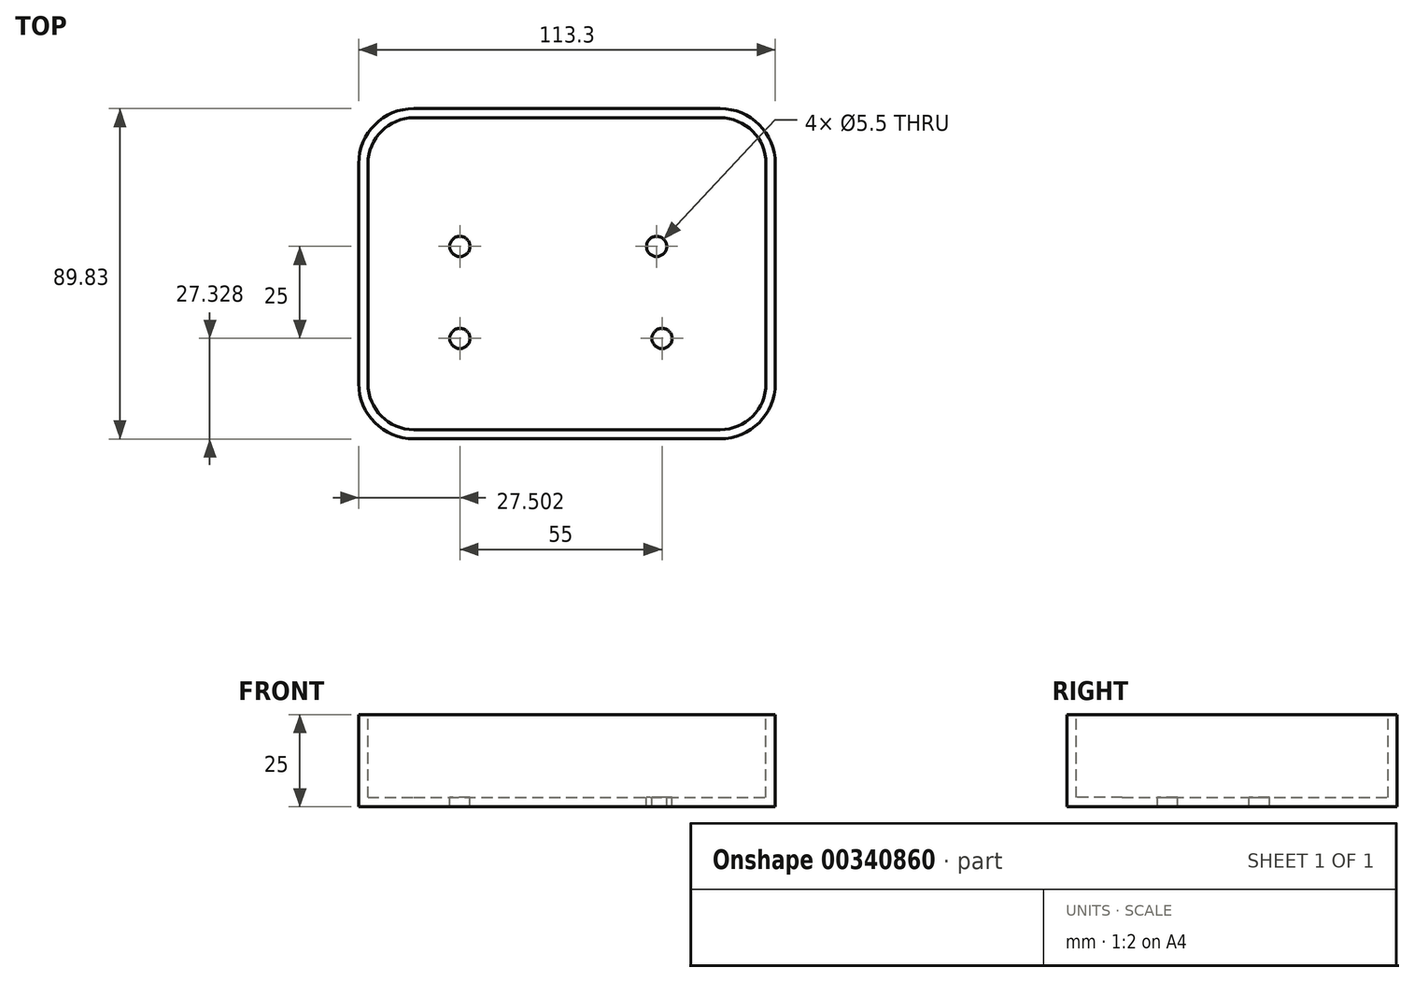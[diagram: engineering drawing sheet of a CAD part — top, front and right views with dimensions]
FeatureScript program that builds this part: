
annotation { "Feature Type Name" : "Feature", "Feature Type Description" : "" }
export const myFeature = defineFeature(function(context is Context, id is Id, definition is map)
    precondition{}
    {
        {
            var Q0;
            Q0=qCreatedBy(makeId("Top.planeOp"),FACE);
            var sketch = newSketch(context, id + "F0", { "sketchPlane" : qUnion([Q0])});
            skLineSegment(sketch, "E0.bottom", {"start": v(-59.12, -58.55) * mm, "end": v(54.18, -58.55) * mm});
            skLineSegment(sketch, "E0.top", {"start": v(-59.12, 31.28) * mm, "end": v(54.18, 31.28) * mm});
            skLineSegment(sketch, "E0.left", {"start": v(-59.12, -58.55) * mm, "end": v(-59.12, 31.28) * mm});
            skLineSegment(sketch, "E0.right", {"start": v(54.18, -58.55) * mm, "end": v(54.18, 31.28) * mm});
            skSolve(sketch);
        }
        {
            var Q0;
            Q0=makeQuery(id+"F0.imprint","IMPRINT",FACE,{"disambiguationData":[TD([[makeQuery(id+"F0.imprint","IMPRINT",EDGE,{"derivedFrom":sQuery(id+"F0.wireOp",EDGE,"E0.bottom")}),1.0]])]});
            extrude(context, id + "F1", {"entities" : qUnion([Q0]), "depth" : 25 * mm, "offsetDistance" : 25 * mm});
        }
        {
            var Q0;
            Q0=makeQuery(id+"F1.opExtrude","SWEPT_EDGE",EDGE,{"disambiguationData":[OSD([sQuery(id+"F0.wireOp",EDGE,"E0.bottom"),sQuery(id+"F0.wireOp",EDGE,"E0.left")])]});
            var Q1;
            Q1=makeQuery(id+"F1.opExtrude","SWEPT_EDGE",EDGE,{"disambiguationData":[OSD([sQuery(id+"F0.wireOp",EDGE,"E0.bottom"),sQuery(id+"F0.wireOp",EDGE,"E0.right")])]});
            var Q2;
            Q2=makeQuery(id+"F1.opExtrude","SWEPT_EDGE",EDGE,{"disambiguationData":[OSD([sQuery(id+"F0.wireOp",EDGE,"E0.top"),sQuery(id+"F0.wireOp",EDGE,"E0.right")])]});
            var Q3;
            Q3=makeQuery(id+"F1.opExtrude","SWEPT_EDGE",EDGE,{"disambiguationData":[OSD([sQuery(id+"F0.wireOp",EDGE,"E0.top"),sQuery(id+"F0.wireOp",EDGE,"E0.left")])]});
            fillet(context, id + "F2", {"entities" : qUnion([Q0, Q1, Q2, Q3]), "radius" : 15 * mm, "tangentPropagation" : true, "allowEdgeOverflow" : false});
        }
        {
            var Q0;
            Q0=makeQuery(id+"F1.opExtrude","CAP_FACE",FACE,{"disambiguationData":[OSD([sQuery(id+"F0.wireOp",EDGE,"E0.bottom"),sQuery(id+"F0.wireOp",EDGE,"E0.top"),sQuery(id+"F0.wireOp",EDGE,"E0.left"),sQuery(id+"F0.wireOp",EDGE,"E0.right")])],"isStart":false});
            shell(context, id + "F3", {"entities" : qUnion([Q0]), "thickness" : 2.5 * mm});
        }
        {
            var Q0;
            Q0=makeQuery(id+"F3.opShell","OFFSET_FACE",FACE,{"disambiguationData":[OSD([sQuery(id+"F0.wireOp",EDGE,"E0.bottom"),sQuery(id+"F0.wireOp",EDGE,"E0.top"),sQuery(id+"F0.wireOp",EDGE,"E0.left"),sQuery(id+"F0.wireOp",EDGE,"E0.right")])]});
            var sketch = newSketch(context, id + "F4", { "sketchPlane" : qUnion([Q0])});
            skPoint(sketch, "E1", {"position": v(-31.62, -6.22) * mm});
            skPoint(sketch, "E2", {"position": v(21.9, -6.22) * mm});
            skPoint(sketch, "E3", {"position": v(-31.62, -31.22) * mm});
            skPoint(sketch, "E4", {"position": v(23.38, -31.22) * mm});
            skSolve(sketch);
        }
        {
            var Q0;
            Q0=sQuery(id+"F4.wireOp",VERTEX,"E1");
            var Q1;
            Q1=sQuery(id+"F4.wireOp",VERTEX,"E3");
            var Q2;
            Q2=sQuery(id+"F4.wireOp",VERTEX,"E2");
            var Q3;
            Q3=sQuery(id+"F4.wireOp",VERTEX,"E4");
            var Q4;
            Q4=makeQuery(id+"F1.opExtrude","SWEPT_BODY",BODY,{"disambiguationData":[OSD([sQuery(id+"F0.wireOp",EDGE,"E0.bottom"),sQuery(id+"F0.wireOp",EDGE,"E0.top"),sQuery(id+"F0.wireOp",EDGE,"E0.left"),sQuery(id+"F0.wireOp",EDGE,"E0.right")])]});
            hole(context, id + "F5", {"style" : HoleStyle.SIMPLE, "endStyle" : HoleEndStyle.THROUGH, "standardTappedOrClearance" : lookupTablePath({ "standard" : "ISO", "fit" : "Normal", "size" : "M5", "type" : "Clearance" }), "standardBlindInLast" : lookupTablePath({ "fit" : "Standard", "standard" : "ISO", "size" : "M5", "type" : "Clearance" }), "holeDiameter" : 5.5 * mm, "majorDiameter" : 5 * mm, "isTappedThrough" : true, "tappedDepth" : 12 * mm, "tapClearance" : 3, "locations" : qUnion([Q0, Q1, Q2, Q3]), "scope" : qUnion([Q4])});
        }
    });
